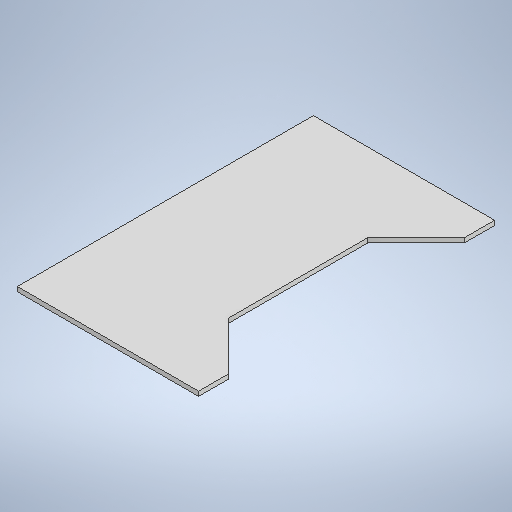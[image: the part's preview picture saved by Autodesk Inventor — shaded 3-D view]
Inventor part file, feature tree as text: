
AUTODESK INVENTOR PART (.ipt)
format: ipt  version: 2025.1 (Build 291241000, 241)  size: 229,376 bytes
history: native  units: mm
features: other x1, extrude x1, sketch x1
ambient origin geometry x8: Origin, YZ Plane, XZ Plane, XY Plane, X Axis, Y Axis, Z Axis, Center Point
bodies: Body1 (feature_tree)
feature tree (3):
  other  "ソリッド1"
  extrude  "押し出し1"  Depth=98.0mm
  sketch  "スケッチ1"
